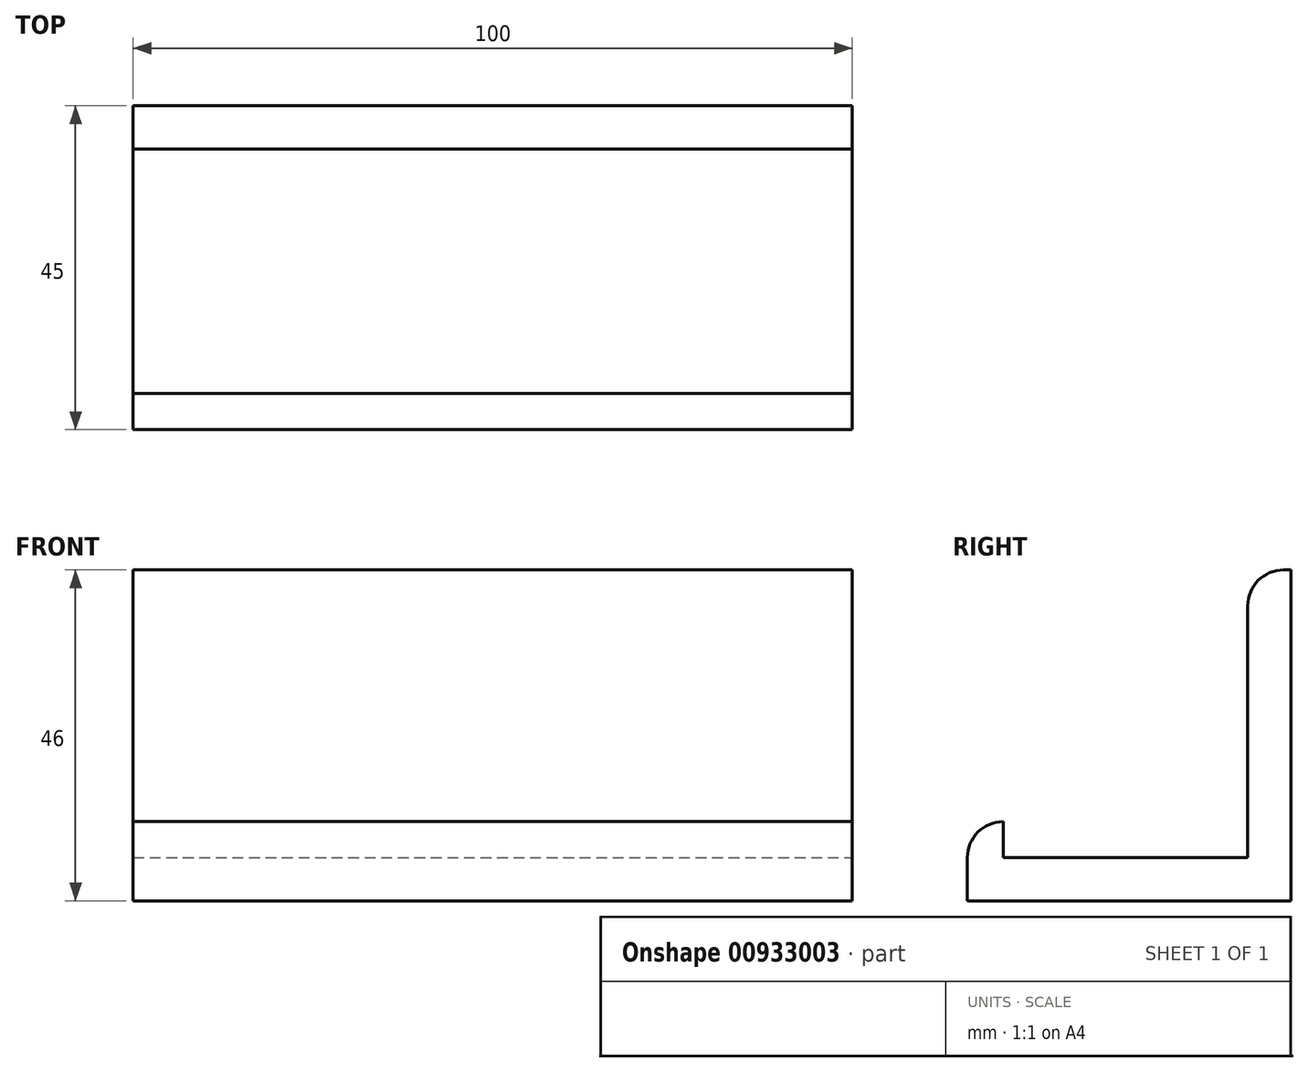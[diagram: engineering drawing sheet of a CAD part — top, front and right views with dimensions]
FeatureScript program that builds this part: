
annotation { "Feature Type Name" : "Feature", "Feature Type Description" : "" }
export const myFeature = defineFeature(function(context is Context, id is Id, definition is map)
    precondition{}
    {
        {
            var Q0;
            Q0=qCreatedBy(makeId("Top.planeOp"),FACE);
            var sketch = newSketch(context, id + "F0", { "sketchPlane" : qUnion([Q0])});
            skLineSegment(sketch, "E0.bottom", {"start": v(50, 22.5) * mm, "end": v(-50, 22.5) * mm});
            skLineSegment(sketch, "E0.top", {"start": v(50, -22.5) * mm, "end": v(-50, -22.5) * mm});
            skLineSegment(sketch, "E0.left", {"start": v(50, 22.5) * mm, "end": v(50, -22.5) * mm});
            skLineSegment(sketch, "E0.right", {"start": v(-50, 22.5) * mm, "end": v(-50, -22.5) * mm});
            skPoint(sketch, "E0.middle", {"position": v(0, 0) * mm});
            skSolve(sketch);
        }
        {
            var Q0;
            Q0=makeQuery(id+"F0.imprint","IMPRINT",FACE,{"disambiguationData":[TD([[makeQuery(id+"F0.imprint","IMPRINT",EDGE,{"derivedFrom":sQuery(id+"F0.wireOp",EDGE,"E0.bottom")}),1.0]])]});
            extrude(context, id + "F1", {"entities" : qUnion([Q0]), "depth" : 6 * mm, "offsetDistance" : 25 * mm});
        }
        {
            var Q0;
            Q0=makeQuery(id+"F1.opExtrude","CAP_FACE",FACE,{"disambiguationData":[OSD([sQuery(id+"F0.wireOp",EDGE,"E0.bottom"),sQuery(id+"F0.wireOp",EDGE,"E0.top"),sQuery(id+"F0.wireOp",EDGE,"E0.left"),sQuery(id+"F0.wireOp",EDGE,"E0.right")])],"isStart":false});
            var sketch = newSketch(context, id + "F2", { "sketchPlane" : qUnion([Q0])});
            skLineSegment(sketch, "E1.bottom", {"start": v(-50, -22.5) * mm, "end": v(-50, -22.5) * mm});
            skLineSegment(sketch, "E1.top", {"start": v(-50, -17.5) * mm, "end": v(-50, -17.5) * mm});
            skLineSegment(sketch, "E1.left", {"start": v(-50, -22.5) * mm, "end": v(-50, -17.5) * mm});
            skLineSegment(sketch, "E1.right", {"start": v(-50, -22.5) * mm, "end": v(-50, -17.5) * mm});
            skLineSegment(sketch, "E2.bottom", {"start": v(50, -17.5) * mm, "end": v(50, -17.5) * mm});
            skLineSegment(sketch, "E2.top", {"start": v(50, -22.5) * mm, "end": v(50, -22.5) * mm});
            skLineSegment(sketch, "E2.left", {"start": v(50, -17.5) * mm, "end": v(50, -22.5) * mm});
            skLineSegment(sketch, "E2.right", {"start": v(50, -17.5) * mm, "end": v(50, -22.5) * mm});
            skLineSegment(sketch, "E3.bottom", {"start": v(-50, -22.5) * mm, "end": v(50, -22.5) * mm});
            skLineSegment(sketch, "E3.top", {"start": v(-50, -17.5) * mm, "end": v(50, -17.5) * mm});
            skLineSegment(sketch, "E3.right", {"start": v(50, -22.5) * mm, "end": v(50, -17.5) * mm});
            skSolve(sketch);
        }
        {
            var Q0;
            Q0=makeQuery(id+"F2.imprint","IMPRINT",FACE,{"disambiguationData":[TD([[makeQuery(id+"F2.imprint","IMPRINT",EDGE,{"derivedFrom":sQuery(id+"F2.wireOp",EDGE,"E3.bottom")}),-1.0]])]});
            extrude(context, id + "F3", {"entities" : qUnion([Q0]), "operationType" : NewBodyOperationType.ADD, "depth" : 5 * mm, "offsetDistance" : 25 * mm});
        }
        {
            var Q0;
            Q0=makeQuery(id+"F1.opExtrude","CAP_FACE",FACE,{"disambiguationData":[OSD([sQuery(id+"F0.wireOp",EDGE,"E0.bottom"),sQuery(id+"F0.wireOp",EDGE,"E0.top"),sQuery(id+"F0.wireOp",EDGE,"E0.left"),sQuery(id+"F0.wireOp",EDGE,"E0.right")])],"isStart":false});
            var sketch = newSketch(context, id + "F4", { "sketchPlane" : qUnion([Q0])});
            skLineSegment(sketch, "E4", {"start": v(-50, 22.5) * mm, "end": v(-50, 16.5) * mm});
            skLineSegment(sketch, "E5", {"start": v(-50, 16.5) * mm, "end": v(50, 16.5) * mm});
            skLineSegment(sketch, "E6", {"start": v(50, 16.5) * mm, "end": v(50, 22.5) * mm});
            skLineSegment(sketch, "E7", {"start": v(50, 22.5) * mm, "end": v(-50, 22.5) * mm});
            skSolve(sketch);
        }
        {
            var Q0;
            Q0=makeQuery(id+"F4.imprint","IMPRINT",FACE,{"disambiguationData":[TD([[makeQuery(id+"F4.imprint","IMPRINT",EDGE,{"derivedFrom":sQuery(id+"F4.wireOp",EDGE,"E4")}),1.0]])]});
            extrude(context, id + "F5", {"entities" : qUnion([Q0]), "operationType" : NewBodyOperationType.ADD, "depth" : 40 * mm, "offsetDistance" : 25 * mm});
        }
        {
            var Q0;
            Q0=makeQuery(id+"F3.opExtrude","CAP_EDGE",EDGE,{"disambiguationData":[OSD([sQuery(id+"F2.wireOp",EDGE,"E3.bottom")])],"isStart":false});
            fillet(context, id + "F6", {"entities" : qUnion([Q0]), "radius" : 5 * mm, "tangentPropagation" : true, "allowEdgeOverflow" : false});
        }
        {
            var Q0;
            Q0=makeQuery(id+"F5.opExtrude","CAP_EDGE",EDGE,{"disambiguationData":[OSD([sQuery(id+"F4.wireOp",EDGE,"E5")])],"isStart":false});
            fillet(context, id + "F7", {"entities" : qUnion([Q0]), "radius" : 5 * mm, "tangentPropagation" : true, "allowEdgeOverflow" : false});
        }
    });
